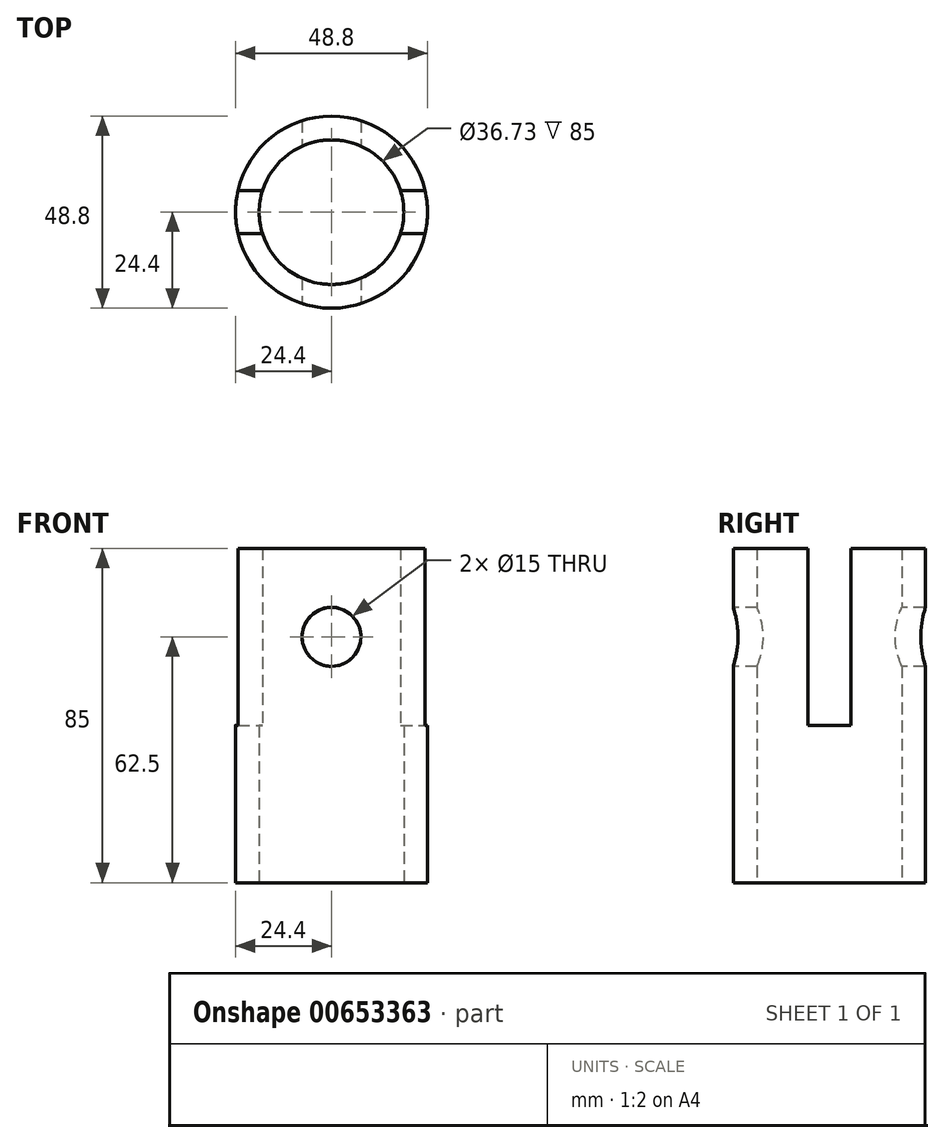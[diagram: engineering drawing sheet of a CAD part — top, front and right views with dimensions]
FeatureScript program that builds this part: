
annotation { "Feature Type Name" : "Feature", "Feature Type Description" : "" }
export const myFeature = defineFeature(function(context is Context, id is Id, definition is map)
    precondition{}
    {
        {
            var Q0;
            Q0=qCreatedBy(makeId("Top.planeOp"),FACE);
            var sketch = newSketch(context, id + "F0", { "sketchPlane" : qUnion([Q0])});
            skCircle(sketch, "E0", {"center": v(0, 0) * mm, "radius": 24.4 * mm});
            skCircle(sketch, "E1", {"center": v(0, 0) * mm, "radius": 18.37 * mm});
            skSolve(sketch);
        }
        {
            var Q0;
            Q0 = qSketchRegion(id + "F0", true);
            extrude(context, id + "F1", {"entities" : qUnion([Q0]), "depth" : 60 * mm, "offsetDistance" : 25 * mm});
        }
        {
            var Q0;
            Q0=qCreatedBy(makeId("Top.planeOp"),FACE);
            var sketch = newSketch(context, id + "F2", { "sketchPlane" : qUnion([Q0])});
            skCircle(sketch, "E2.0", {"center": v(0, 0) * mm, "radius": 24.4 * mm});
            skCircle(sketch, "E3.0", {"center": v(0, 0) * mm, "radius": 18.37 * mm});
            skSolve(sketch);
        }
        {
            var Q0;
            Q0 = qSketchRegion(id + "F2", true);
            extrude(context, id + "F3", {"entities" : qUnion([Q0]), "operationType" : NewBodyOperationType.ADD, "oppositeDirection" : true, "depth" : 25 * mm, "offsetDistance" : 25 * mm});
        }
        {
            var Q0;
            Q0=qCreatedBy(makeId("Right.planeOp"),FACE);
            var sketch = newSketch(context, id + "F4", { "sketchPlane" : qUnion([Q0])});
            skLineSegment(sketch, "E4.0", {"start": v(-5.5, 60) * mm, "end": v(5.5, 60) * mm, "construction": true});
            skLineSegment(sketch, "E5.bottom", {"start": v(0, 60) * mm, "end": v(-5.5, 60) * mm});
            skLineSegment(sketch, "E5.top", {"start": v(0, 15) * mm, "end": v(-5.5, 15) * mm});
            skLineSegment(sketch, "E5.right", {"start": v(-5.5, 60) * mm, "end": v(-5.5, 15) * mm});
            skLineSegment(sketch, "E6.MirrorCS", {"start": v(5.5, 60) * mm, "end": v(5.5, 15) * mm});
            skLineSegment(sketch, "E7.MirrorCS", {"start": v(0, 15) * mm, "end": v(5.5, 15) * mm});
            skPoint(sketch, "E8.orphan", {"position": v(24.4, 60) * mm});
            skPoint(sketch, "E9.orphan", {"position": v(-24.4, 60) * mm});
            skLineSegment(sketch, "E10", {"start": v(-5.5, 60) * mm, "end": v(5.5, 60) * mm});
            skSolve(sketch);
        }
        {
            var Q0;
            Q0 = qSketchRegion(id + "F4", true);
            extrude(context, id + "F5", {"entities" : qUnion([Q0]), "operationType" : NewBodyOperationType.REMOVE, "endBound" : BoundingType.THROUGH_ALL, "oppositeDirection" : true, "depth" : 25 * mm, "offsetDistance" : 25 * mm, "hasSecondDirection" : true, "secondDirectionBound" : BoundingType.THROUGH_ALL, "secondDirectionOppositeDirection" : false, "secondDirectionDepth" : 25 * mm});
        }
        {
            var Q0;
            Q0=qCreatedBy(makeId("Front.planeOp"),FACE);
            var sketch = newSketch(context, id + "F6", { "sketchPlane" : qUnion([Q0])});
            skLineSegment(sketch, "E11.0", {"start": v(-23.77, 60) * mm, "end": v(23.77, 60) * mm, "construction": true});
            skLineSegment(sketch, "E12", {"start": v(0, 0) * mm, "end": v(0, 70.78) * mm, "construction": true});
            skCircle(sketch, "E13", {"center": v(0, 37.5) * mm, "radius": 7.5 * mm});
            skSolve(sketch);
        }
        {
            var Q0;
            Q0 = qSketchRegion(id + "F6", true);
            extrude(context, id + "F7", {"entities" : qUnion([Q0]), "operationType" : NewBodyOperationType.REMOVE, "endBound" : BoundingType.THROUGH_ALL, "oppositeDirection" : true, "depth" : 25 * mm, "offsetDistance" : 25 * mm, "hasSecondDirection" : true, "secondDirectionBound" : BoundingType.THROUGH_ALL, "secondDirectionOppositeDirection" : false, "secondDirectionDepth" : 25 * mm});
        }
    });
